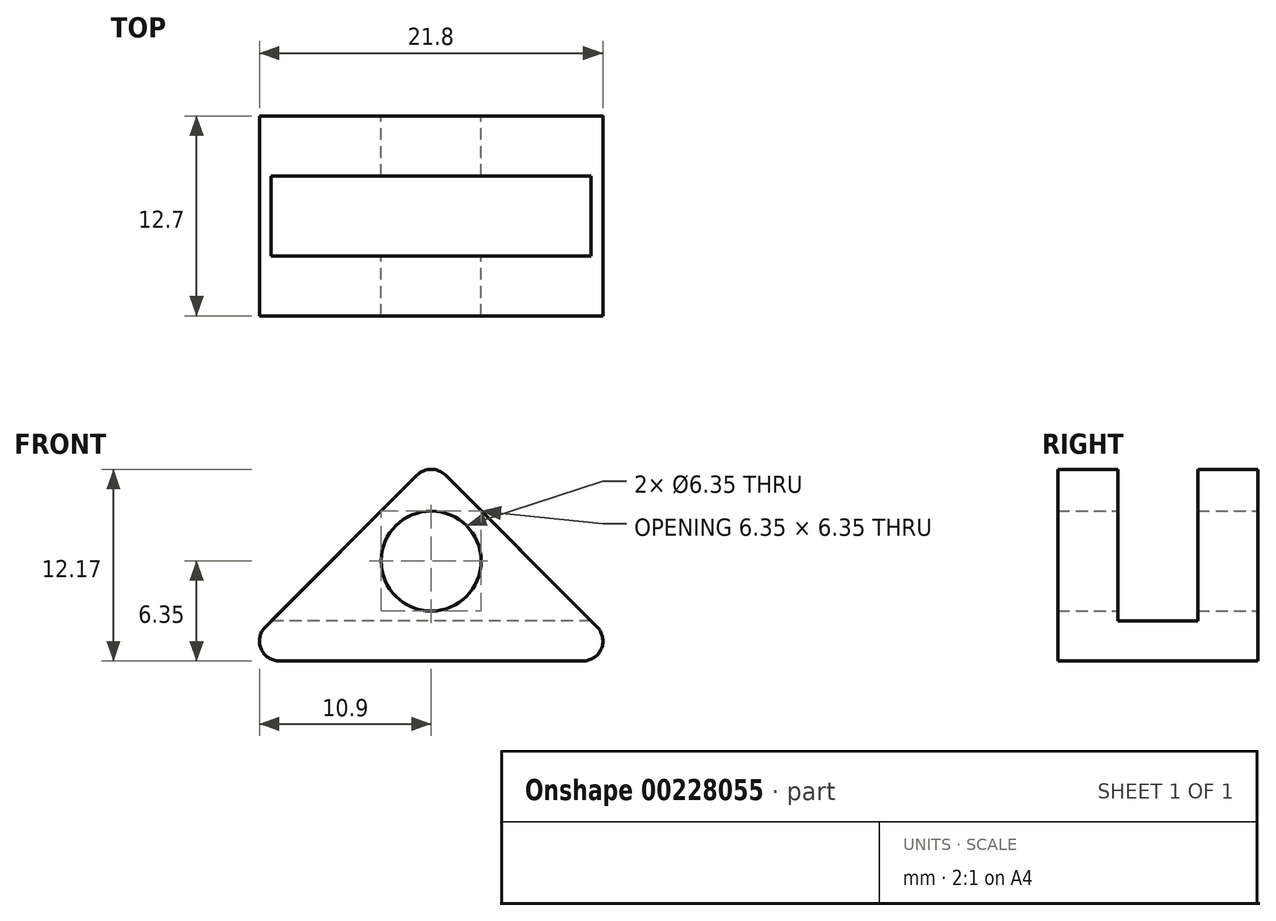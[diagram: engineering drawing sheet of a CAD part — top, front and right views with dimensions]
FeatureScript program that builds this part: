
annotation { "Feature Type Name" : "Feature", "Feature Type Description" : "" }
export const myFeature = defineFeature(function(context is Context, id is Id, definition is map)
    precondition{}
    {
        {
            var Q0;
            Q0=qCreatedBy(makeId("Front.planeOp"),FACE);
            var sketch = newSketch(context, id + "F0", { "sketchPlane" : qUnion([Q0])});
            skLineSegment(sketch, "E0", {"start": v(0, 0) * mm, "end": v(25.4, 0) * mm});
            skLineSegment(sketch, "E1", {"start": v(25.4, 0) * mm, "end": v(12.7, 12.7) * mm});
            skLineSegment(sketch, "E2", {"start": v(12.7, 12.7) * mm, "end": v(0, 0) * mm});
            skCircle(sketch, "E3", {"center": v(12.7, 6.35) * mm, "radius": 3.18 * mm});
            skLineSegment(sketch, "E4", {"start": v(12.7, 12.7) * mm, "end": v(12.7, 0) * mm, "construction": true});
            skSolve(sketch);
        }
        {
            var Q0;
            Q0 = qSketchRegion(id + "F0", true);
            extrude(context, id + "F1", {"entities" : qUnion([Q0]), "depth" : 12.7 * mm, "offsetDistance" : 25.4 * mm});
        }
        {
            var Q0;
            Q0=qCreatedBy(makeId("Right.planeOp"),FACE);
            var sketch = newSketch(context, id + "F2", { "sketchPlane" : qUnion([Q0])});
            skLineSegment(sketch, "E5.bottom", {"start": v(-3.81, 12.7) * mm, "end": v(-8.9, 12.7) * mm});
            skLineSegment(sketch, "E5.top", {"start": v(-3.81, 2.54) * mm, "end": v(-8.9, 2.54) * mm});
            skLineSegment(sketch, "E5.left", {"start": v(-3.81, 12.7) * mm, "end": v(-3.81, 2.54) * mm});
            skLineSegment(sketch, "E5.right", {"start": v(-8.9, 12.7) * mm, "end": v(-8.9, 2.54) * mm});
            skLineSegment(sketch, "E6", {"start": v(-3.81, 2.54) * mm, "end": v(0, 0) * mm, "construction": true});
            skLineSegment(sketch, "E7", {"start": v(-8.9, 2.54) * mm, "end": v(-12.7, 0) * mm, "construction": true});
            skSolve(sketch);
        }
        {
            var Q0;
            Q0 = qSketchRegion(id + "F2", true);
            extrude(context, id + "F3", {"entities" : qUnion([Q0]), "operationType" : NewBodyOperationType.REMOVE, "endBound" : BoundingType.THROUGH_ALL, "depth" : 25.4 * mm, "offsetDistance" : 25.4 * mm});
        }
        {
            var Q0;
            {var subQ0=sQuery(id+"F0.wireOp",EDGE,"E2");var subQ1=sQuery(id+"F0.wireOp",EDGE,"E1");Q0=makeQuery(id+"F3.boolean.opBoolean","SPLIT",EDGE,{"disambiguationData":[TD([makeQuery(id+"F3.opExtrude","SWEPT_FACE",FACE,{"disambiguationData":[OSD([sQuery(id+"F2.wireOp",EDGE,"E5.left")])]})])],"derivedFrom":makeQuery(id+"F1.opExtrude","SWEPT_EDGE",EDGE,{"disambiguationData":[OSD([subQ1,subQ0])]})});}
            var Q1;
            {var subQ0=sQuery(id+"F0.wireOp",EDGE,"E2");var subQ1=sQuery(id+"F0.wireOp",EDGE,"E1");Q1=makeQuery(id+"F3.boolean.opBoolean","SPLIT",EDGE,{"disambiguationData":[TD([makeQuery(id+"F3.opExtrude","SWEPT_FACE",FACE,{"disambiguationData":[OSD([sQuery(id+"F2.wireOp",EDGE,"E5.right")])]})])],"derivedFrom":makeQuery(id+"F1.opExtrude","SWEPT_EDGE",EDGE,{"disambiguationData":[OSD([subQ1,subQ0])]})});}
            var Q2;
            Q2=makeQuery(id+"F1.opExtrude","SWEPT_EDGE",EDGE,{"disambiguationData":[OSD([sQuery(id+"F0.wireOp",EDGE,"E0"),sQuery(id+"F0.wireOp",EDGE,"E2")])]});
            var Q3;
            Q3=makeQuery(id+"F1.opExtrude","SWEPT_EDGE",EDGE,{"disambiguationData":[OSD([sQuery(id+"F0.wireOp",EDGE,"E0"),sQuery(id+"F0.wireOp",EDGE,"E1")])]});
            fillet(context, id + "F4", {"entities" : qUnion([Q0, Q1, Q2, Q3]), "radius" : 1.27 * mm, "tangentPropagation" : true, "allowEdgeOverflow" : false});
        }
    });
